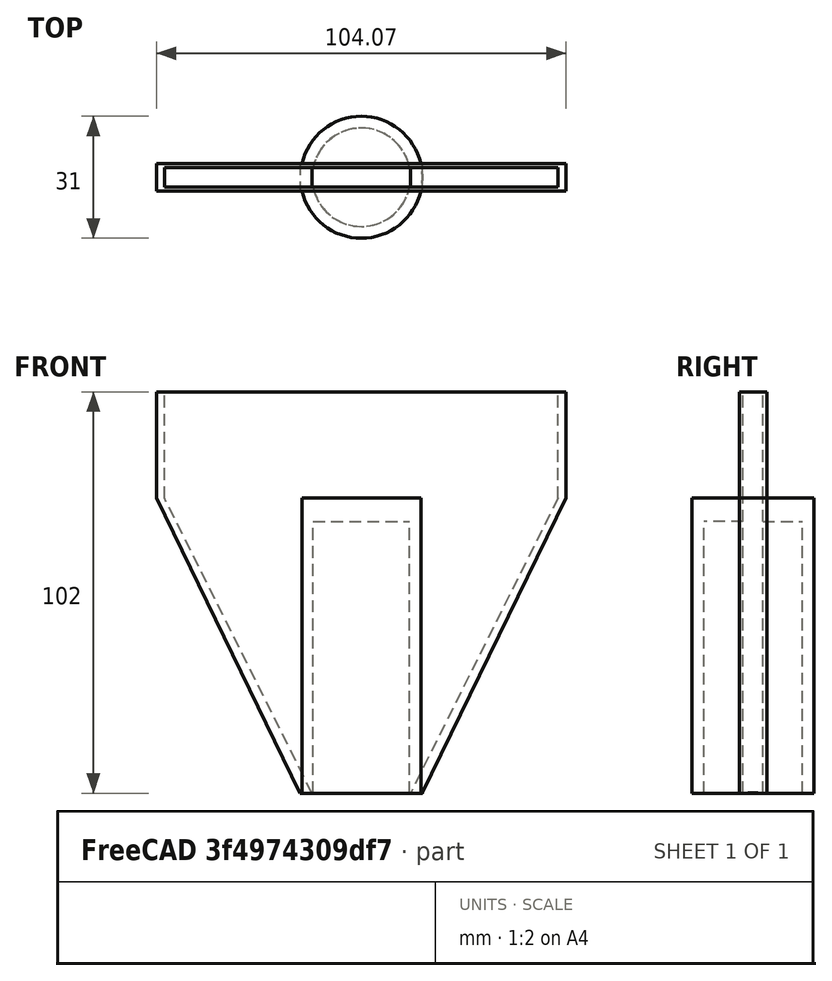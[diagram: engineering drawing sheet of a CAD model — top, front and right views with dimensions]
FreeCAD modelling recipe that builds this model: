
FCSTD DOCUMENT  (FreeCAD 0.16R6045 (Git))
Label: qqqqqqqq
License: All rights reserved
LicenseURL: http://en.wikipedia.org/wiki/All_rights_reserved
objects: Part::Cylinder×2, Part::Box×2, Sketcher::SketchObject×2, PartDesign::Pad×2, Part::MultiFuse×2, Part::Cut×1
note: 13 computed .brp shape members not serialized (recipe doc carries the construction recipe); baked Part::Feature solids carry a one-line shape summary decoded from their .brp

FEATURE [Part::Cylinder] Cylinder  label="hose hole"
  Angle = 360
  Height = 72
  Placement = pos=(0,0,-15.5) rot=(0,0,1;0rad)
  Radius = 12.5
FEATURE [Part::Box] Box  label="tip hole"
  Height = 27
  Length = 100
  Placement = pos=(-50,-2.5,62.5) rot=(0,0,1;0rad)
  Width = 5
FEATURE [Part::Cylinder] Cylinder001  label="hose body"
  Angle = 360
  Height = 75
  Placement = pos=(0,0,-12.5) rot=(0,0,1;0rad)
  Radius = 15.5
FEATURE [Part::Box] Box001  label="tip body"
  Height = 27
  Length = 104
  Placement = pos=(-52,-3.5,62.5) rot=(0,0,1;0rad)
  Width = 7
FEATURE [Sketcher::SketchObject] Sketch  label="internal duct sketch"
  Placement = pos=(-68,0,-12.5) rot=(1,0,0;1.5708rad)
  sketch-geometry (4):
    g0: LineSegment StartX=55.4827 StartY=0 StartZ=0 EndX=17.9827 EndY=75 EndZ=0
    g1: LineSegment StartX=80.4827 StartY=0 StartZ=0 EndX=55.4827 EndY=0 EndZ=0
    g2: LineSegment StartX=17.9827 StartY=75 StartZ=0 EndX=117.983 EndY=75 EndZ=0
    g3: LineSegment StartX=117.983 StartY=75 StartZ=0 EndX=80.4827 EndY=0 EndZ=0
  constraints (6):
    c: PointOnObject(g0,g-1)
    c: Horizontal(g1)
    c: Horizontal(g2)
    c: Coincident(g2,g3)
    c: PointOnObject(g3,g-1)
    c: Coincident(g0,g2)
FEATURE [PartDesign::Pad] Pad  label="internal duct"
  Length = 5
  Length2 = 100
  Midplane = true
  Placement = pos=(-68,0,-12.5) rot=(1,0,0;1.5708rad)
  Sketch = -> Sketch
  Type = 0
FEATURE [Sketcher::SketchObject] Sketch001  label="internal duct wall sketch"
  Placement = pos=(-65.5,0,-12.5) rot=(1,0,0;1.5708rad)
  sketch-geometry (4):
    g0: LineSegment StartX=49.9297 StartY=0 StartZ=0 EndX=13.4297 EndY=75 EndZ=0
    g1: LineSegment StartX=80.9297 StartY=0 StartZ=0 EndX=49.9297 EndY=0 EndZ=0
    g2: LineSegment StartX=13.4297 StartY=75 StartZ=0 EndX=117.43 EndY=75 EndZ=0
    g3: LineSegment StartX=117.43 StartY=75 StartZ=0 EndX=80.9297 EndY=0 EndZ=0
  constraints (6):
    c: PointOnObject(g0,g-1)
    c: Horizontal(g1)
    c: Horizontal(g2)
    c: Coincident(g2,g3)
    c: PointOnObject(g3,g-1)
    c: Coincident(g0,g2)
FEATURE [PartDesign::Pad] Pad001  label="internal duct wall"
  Length = 7
  Length2 = 100
  Midplane = true
  Placement = pos=(-65.5,0,-12.5) rot=(1,0,0;1.5708rad)
  Sketch = -> Sketch001
  Type = 0
FEATURE [Part::MultiFuse] Fusion  label="Holes"
  Shapes = -> [Cylinder,Box,Pad]
FEATURE [Part::MultiFuse] Fusion001  label="Body"
  Shapes = -> [Cylinder001,Box001,Pad001]
FEATURE [Part::Cut] Cut  label="Body with holes"
  Base = -> Fusion001
  Tool = -> Fusion
